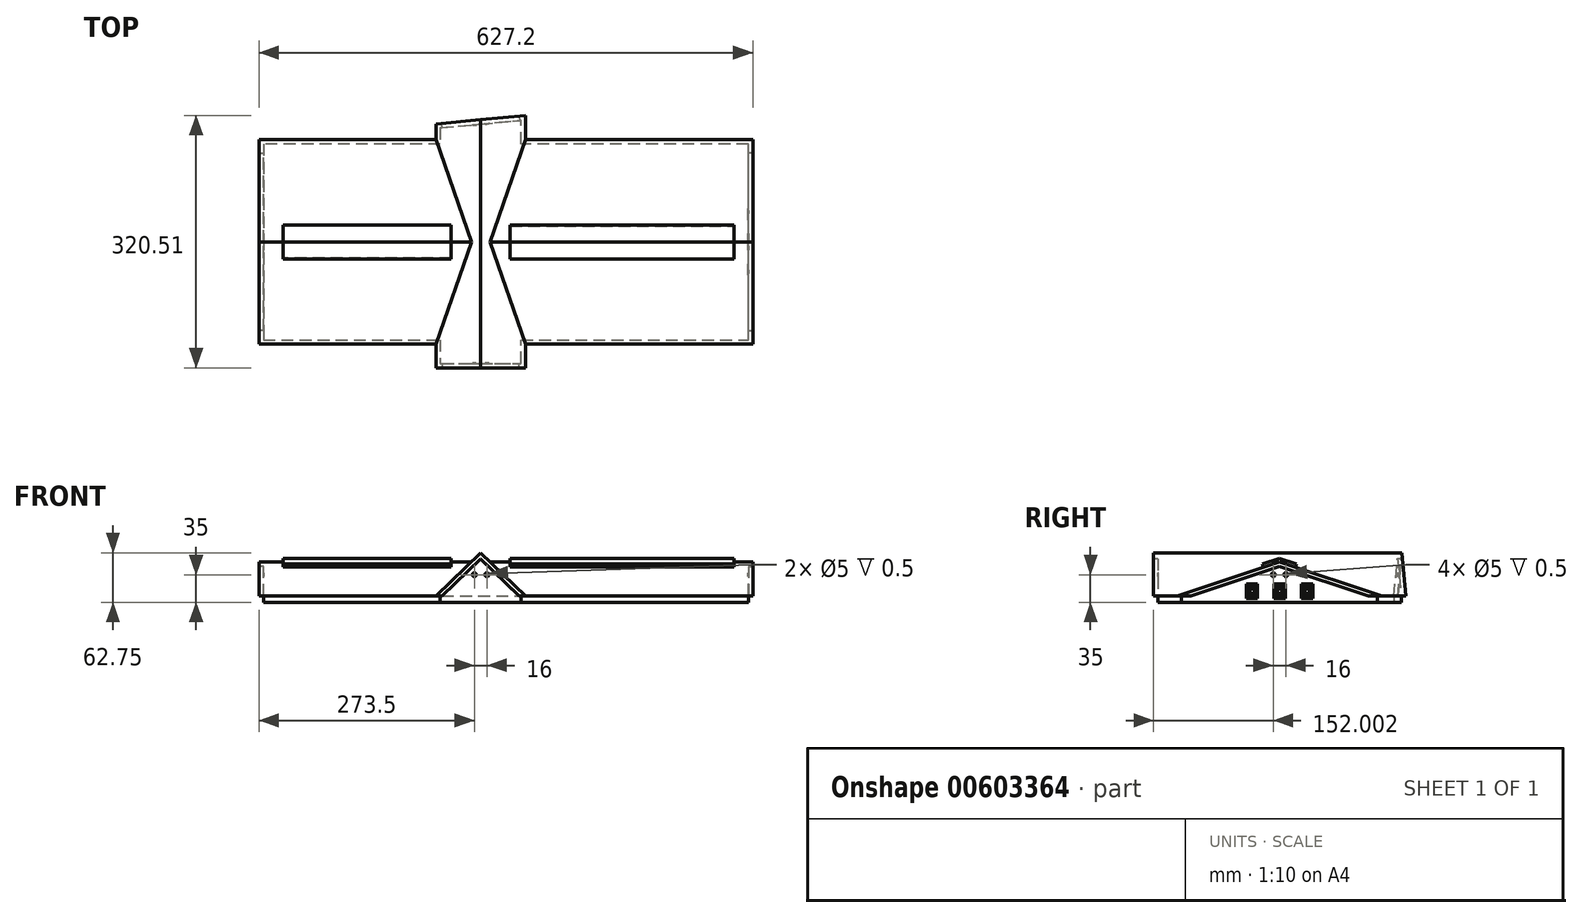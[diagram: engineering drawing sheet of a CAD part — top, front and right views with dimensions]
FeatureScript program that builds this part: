
annotation { "Feature Type Name" : "Feature", "Feature Type Description" : "" }
export const myFeature = defineFeature(function(context is Context, id is Id, definition is map)
    precondition{}
    {
        {
            var Q0;
            Q0=qCreatedBy(makeId("Top.planeOp"),FACE);
            var sketch = newSketch(context, id + "F0", { "sketchPlane" : qUnion([Q0])});
            skLineSegment(sketch, "E0", {"start": v(-327.3, -140.86) * mm, "end": v(-102.6, -140.86) * mm});
            skLineSegment(sketch, "E1", {"start": v(-102.6, -140.86) * mm, "end": v(-102.6, -170.86) * mm});
            skLineSegment(sketch, "E2", {"start": v(-102.6, -170.86) * mm, "end": v(0, -170.86) * mm});
            skLineSegment(sketch, "E3", {"start": v(0, -170.86) * mm, "end": v(0, -140.86) * mm});
            skLineSegment(sketch, "E4", {"start": v(0, -140.86) * mm, "end": v(288.9, -140.86) * mm});
            skLineSegment(sketch, "E5", {"start": v(288.9, -140.86) * mm, "end": v(288.9, 108.14) * mm});
            skLineSegment(sketch, "E6", {"start": v(288.9, 108.14) * mm, "end": v(0, 108.14) * mm});
            skLineSegment(sketch, "E7", {"start": v(0, 108.14) * mm, "end": v(0, 138.14) * mm});
            skLineSegment(sketch, "E8", {"start": v(-102.6, 128.64) * mm, "end": v(-102.6, 108.14) * mm});
            skLineSegment(sketch, "E9", {"start": v(-102.6, 108.14) * mm, "end": v(-327.3, 108.14) * mm});
            skLineSegment(sketch, "E10", {"start": v(-327.3, 108.14) * mm, "end": v(-327.3, -140.86) * mm});
            skLineSegment(sketch, "E11", {"start": v(-102.6, 128.64) * mm, "end": v(0, 138.14) * mm});
            skSolve(sketch);
        }
        {
            var Q0;
            Q0=makeQuery(id+"F0.imprint","IMPRINT",FACE,{"disambiguationData":[TD([[makeQuery(id+"F0.imprint","IMPRINT",EDGE,{"derivedFrom":sQuery(id+"F0.wireOp",EDGE,"E0")}),1.0]])]});
            extrude(context, id + "F1", {"entities" : qUnion([Q0]), "depth" : 8 * mm, "offsetDistance" : 25 * mm});
        }
        {
            var Q0;
            Q0=makeQuery(id+"F1.opExtrude","SWEPT_FACE",FACE,{"disambiguationData":[OSD([sQuery(id+"F0.wireOp",EDGE,"E5")])]});
            var sketch = newSketch(context, id + "F2", { "sketchPlane" : qUnion([Q0])});
            skLineSegment(sketch, "E12", {"start": v(-146.36, 8) * mm, "end": v(113.64, 8) * mm});
            skPoint(sketch, "E13", {"position": v(-140.86, 8) * mm});
            skPoint(sketch, "E14", {"position": v(108.14, 8) * mm});
            skLineSegment(sketch, "E15", {"start": v(-146.36, 8) * mm, "end": v(-16.36, 51.45) * mm});
            skLineSegment(sketch, "E16", {"start": v(-16.36, 51.45) * mm, "end": v(113.64, 8) * mm});
            skPoint(sketch, "E17", {"position": v(-16.36, 8) * mm});
            skSolve(sketch);
        }
        {
            var Q0;
            {var subQ0=sQuery(id+"F2.wireOp",EDGE,"E15");Q0=makeQuery(id+"F2.imprint","IMPRINT",FACE,{"disambiguationData":[TD([[makeQuery(id+"F2.imprint","IMPRINT",EDGE,{"derivedFrom":subQ0}),-1.0]])]});}
            extrude(context, id + "F3", {"entities" : qUnion([Q0]), "operationType" : NewBodyOperationType.ADD, "oppositeDirection" : true, "depth" : (616.2 + 5.5) * mm, "offsetDistance" : 25 * mm});
        }
        {
            var Q0;
            Q0 = qSketchRegion(id + "F2", true);
            extrude(context, id + "F4", {"entities" : qUnion([Q0]), "operationType" : NewBodyOperationType.ADD, "depth" : 5.5 * mm, "offsetDistance" : 25 * mm});
        }
        {
            var Q0;
            Q0=makeQuery(id+"F1.opExtrude","SWEPT_FACE",FACE,{"disambiguationData":[OSD([sQuery(id+"F0.wireOp",EDGE,"E2")])]});
            var sketch = newSketch(context, id + "F5", { "sketchPlane" : qUnion([Q0])});
            skLineSegment(sketch, "E18", {"start": v(-108.1, 8) * mm, "end": v(5.5, 8) * mm});
            skPoint(sketch, "E19", {"position": v(-102.6, 8) * mm});
            skPoint(sketch, "E20", {"position": v(0, 8) * mm});
            skPoint(sketch, "E21", {"position": v(-51.3, 8) * mm});
            skLineSegment(sketch, "E22", {"start": v(-51.3, 8) * mm, "end": v(-51.3, 90.85) * mm, "construction": true});
            skPoint(sketch, "E23", {"position": v(-51.3, 62.75) * mm});
            skLineSegment(sketch, "E24", {"start": v(-108.1, 8) * mm, "end": v(-51.3, 62.75) * mm});
            skLineSegment(sketch, "E25", {"start": v(-51.3, 62.75) * mm, "end": v(5.5, 8) * mm});
            skSolve(sketch);
        }
        {
            var Q0;
            Q0 = qSketchRegion(id + "F5", true);
            var Q1;
            Q1=makeQuery(id+"F1.opExtrude","SWEPT_FACE",FACE,{"disambiguationData":[OSD([sQuery(id+"F0.wireOp",EDGE,"E11")])]});
            extrude(context, id + "F6", {"entities" : qUnion([Q0]), "operationType" : NewBodyOperationType.ADD, "endBound" : BoundingType.UP_TO_SURFACE, "oppositeDirection" : true, "depth" : 25 * mm, "endBoundEntityFace" : qUnion([Q1]), "hasOffset" : true, "offsetDistance" : -5.5 * mm});
        }
        {
            var Q0;
            Q0 = qSketchRegion(id + "F5", true);
            extrude(context, id + "F7", {"entities" : qUnion([Q0]), "operationType" : NewBodyOperationType.ADD, "depth" : 5.5 * mm, "offsetDistance" : 25 * mm});
        }
        {
            var Q0;
            Q0=makeQuery(id+"F6.opExtrude","CAP_FACE",FACE,{"disambiguationData":[OSD([sQuery(id+"F5.wireOp",EDGE,"E18"),sQuery(id+"F5.wireOp",EDGE,"E24"),sQuery(id+"F5.wireOp",EDGE,"E25")])],"isStart":false});
            var sketch = newSketch(context, id + "F8", { "sketchPlane" : qUnion([Q0])});
            skLineSegment(sketch, "E26.0", {"start": v(38.28, 55.82) * mm, "end": v(-15.3, 4.4) * mm});
            skLineSegment(sketch, "E26.1", {"start": v(91.86, 4.4) * mm, "end": v(38.28, 55.82) * mm});
            skLineSegment(sketch, "E27", {"start": v(-15.3, 4.4) * mm, "end": v(91.86, 4.4) * mm});
            skSolve(sketch);
        }
        {
            var Q0;
            {var subQ0=sQuery(id+"F8.wireOp",EDGE,"E26.1");var subQ1=sQuery(id+"F8.wireOp",EDGE,"E26.0");var subQ2=makeQuery(id+"F8.imprint","INTERSECT",VERTEX,{"derivedFrom":[subQ1,subQ0]});Q0=makeQuery(id+"F8.imprint","IMPRINT",FACE,{"disambiguationData":[TD([[makeQuery(id+"F8.imprint","IMPRINT",EDGE,{"disambiguationData":[TD([[subQ2,-1.0]])],"derivedFrom":subQ1}),1.0]])]});}
            extrude(context, id + "F9", {"entities" : qUnion([Q0]), "operationType" : NewBodyOperationType.REMOVE, "oppositeDirection" : true, "depth" : 5.5 * mm, "offsetDistance" : 25 * mm});
        }
        {
            var Q0;
            Q0=makeQuery(id+"F3.opExtrude","CAP_FACE",FACE,{"disambiguationData":[OSD([sQuery(id+"F2.wireOp",EDGE,"E12"),sQuery(id+"F2.wireOp",EDGE,"E15"),sQuery(id+"F2.wireOp",EDGE,"E16")])],"isStart":false});
            var sketch = newSketch(context, id + "F10", { "sketchPlane" : qUnion([Q0])});
            skLineSegment(sketch, "E28.0", {"start": v(16.36, 45.65) * mm, "end": v(-111.9, 2.78) * mm});
            skLineSegment(sketch, "E28.1", {"start": v(144.61, 2.78) * mm, "end": v(16.36, 45.65) * mm});
            skLineSegment(sketch, "E29", {"start": v(-111.9, 2.78) * mm, "end": v(144.61, 2.78) * mm});
            skSolve(sketch);
        }
        {
            var Q0;
            Q0 = qSketchRegion(id + "F10", true);
            extrude(context, id + "F11", {"entities" : qUnion([Q0]), "operationType" : NewBodyOperationType.REMOVE, "oppositeDirection" : true, "depth" : 5.5 * mm, "offsetDistance" : 25 * mm});
        }
        {
            var Q0;
            Q0=makeQuery(id+"F4.opExtrude","CAP_FACE",FACE,{"disambiguationData":[OSD([sQuery(id+"F2.wireOp",EDGE,"E12"),sQuery(id+"F2.wireOp",EDGE,"E15"),sQuery(id+"F2.wireOp",EDGE,"E16")])],"isStart":false});
            var sketch = newSketch(context, id + "F12", { "sketchPlane" : qUnion([Q0])});
            skLineSegment(sketch, "E30.0", {"start": v(-16.36, 45.65) * mm, "end": v(111.9, 2.78) * mm});
            skLineSegment(sketch, "E30.1", {"start": v(-144.61, 2.78) * mm, "end": v(-16.36, 45.65) * mm});
            skLineSegment(sketch, "E31", {"start": v(-144.61, 2.78) * mm, "end": v(111.9, 2.78) * mm});
            skSolve(sketch);
        }
        {
            var Q0;
            Q0 = qSketchRegion(id + "F12", true);
            extrude(context, id + "F13", {"entities" : qUnion([Q0]), "operationType" : NewBodyOperationType.REMOVE, "oppositeDirection" : true, "depth" : 5.5 * mm, "offsetDistance" : 25 * mm});
        }
        {
            var Q0;
            Q0=makeQuery(id+"F7.opExtrude","CAP_FACE",FACE,{"disambiguationData":[OSD([sQuery(id+"F5.wireOp",EDGE,"E18"),sQuery(id+"F5.wireOp",EDGE,"E24"),sQuery(id+"F5.wireOp",EDGE,"E25")])],"isStart":false});
            var sketch = newSketch(context, id + "F14", { "sketchPlane" : qUnion([Q0])});
            skLineSegment(sketch, "E32.0", {"start": v(-51.3, 55.11) * mm, "end": v(1.68, 4.04) * mm});
            skLineSegment(sketch, "E32.1", {"start": v(-104.28, 4.04) * mm, "end": v(-51.3, 55.11) * mm});
            skLineSegment(sketch, "E33", {"start": v(-104.28, 4.04) * mm, "end": v(1.68, 4.04) * mm});
            skSolve(sketch);
        }
        {
            var Q0;
            Q0 = qSketchRegion(id + "F14", true);
            extrude(context, id + "F15", {"entities" : qUnion([Q0]), "operationType" : NewBodyOperationType.REMOVE, "oppositeDirection" : true, "depth" : 5.5 * mm, "offsetDistance" : 25 * mm});
        }
        {
            var Q0;
            Q0=makeQuery(id+"F4.opExtrude","CAP_FACE",FACE,{"disambiguationData":[OSD([sQuery(id+"F2.wireOp",EDGE,"E12"),sQuery(id+"F2.wireOp",EDGE,"E15"),sQuery(id+"F2.wireOp",EDGE,"E16")])],"isStart":false});
            var sketch = newSketch(context, id + "F16", { "sketchPlane" : qUnion([Q0])});
            skLineSegment(sketch, "E34", {"start": v(-36.64, 44.67) * mm, "end": v(-16.36, 51.45) * mm});
            skLineSegment(sketch, "E35", {"start": v(-16.36, 51.45) * mm, "end": v(3.93, 44.67) * mm});
            skLineSegment(sketch, "E36.0", {"start": v(-16.36, 55.67) * mm, "end": v(5.2, 48.47) * mm});
            skLineSegment(sketch, "E36.1", {"start": v(-37.91, 48.47) * mm, "end": v(-16.36, 55.67) * mm});
            skLineSegment(sketch, "E37", {"start": v(-37.91, 48.47) * mm, "end": v(-36.64, 44.67) * mm});
            skLineSegment(sketch, "E38", {"start": v(5.2, 48.47) * mm, "end": v(3.93, 44.67) * mm});
            skSolve(sketch);
        }
        {
            var Q0;
            Q0=makeQuery(id+"F16.imprint","IMPRINT",FACE,{"disambiguationData":[TD([[makeQuery(id+"F16.imprint","IMPRINT",EDGE,{"derivedFrom":sQuery(id+"F16.wireOp",EDGE,"E34")}),1.0]])]});
            extrude(context, id + "F17", {"entities" : qUnion([Q0]), "operationType" : NewBodyOperationType.ADD, "oppositeDirection" : true, "depth" : (30.35 + 277.85) * mm, "offsetDistance" : 25 * mm});
        }
        {
            var Q0;
            Q0 = qSketchRegion(id + "F16", true);
            extrude(context, id + "F18", {"entities" : qUnion([Q0]), "operationType" : NewBodyOperationType.REMOVE, "oppositeDirection" : true, "depth" : 24 * mm, "offsetDistance" : 25 * mm});
        }
        {
            var Q0;
            Q0=makeQuery(id+"F3.opExtrude","CAP_FACE",FACE,{"disambiguationData":[OSD([sQuery(id+"F2.wireOp",EDGE,"E12"),sQuery(id+"F2.wireOp",EDGE,"E15"),sQuery(id+"F2.wireOp",EDGE,"E16")])],"isStart":false});
            var sketch = newSketch(context, id + "F19", { "sketchPlane" : qUnion([Q0])});
            skLineSegment(sketch, "E39", {"start": v(-3.93, 44.67) * mm, "end": v(16.36, 51.45) * mm});
            skLineSegment(sketch, "E40", {"start": v(16.36, 51.45) * mm, "end": v(36.64, 44.67) * mm});
            skLineSegment(sketch, "E41.0", {"start": v(16.36, 55.67) * mm, "end": v(37.91, 48.47) * mm});
            skLineSegment(sketch, "E41.1", {"start": v(-5.2, 48.47) * mm, "end": v(16.36, 55.67) * mm});
            skLineSegment(sketch, "E42", {"start": v(-5.2, 48.47) * mm, "end": v(-3.93, 44.67) * mm});
            skLineSegment(sketch, "E43", {"start": v(37.91, 48.47) * mm, "end": v(36.64, 44.67) * mm});
            skSolve(sketch);
        }
        {
            var Q0;
            Q0 = qSketchRegion(id + "F19", true);
            extrude(context, id + "F20", {"entities" : qUnion([Q0]), "operationType" : NewBodyOperationType.ADD, "oppositeDirection" : true, "depth" : (30.35 + 213.85) * mm, "offsetDistance" : 25 * mm});
        }
        {
            var Q0;
            Q0 = qSketchRegion(id + "F19", true);
            extrude(context, id + "F21", {"entities" : qUnion([Q0]), "operationType" : NewBodyOperationType.REMOVE, "oppositeDirection" : true, "depth" : 30.35 * mm, "offsetDistance" : 25 * mm});
        }
        {
            var Q0;
            Q0=makeQuery(id+"F11.boolean.opBoolean","MERGE",FACE,{"derivedFrom":[makeQuery(id+"F1.opExtrude","SWEPT_FACE",FACE,{"disambiguationData":[OSD([sQuery(id+"F0.wireOp",EDGE,"E10")])]}),makeQuery(id+"F11.opExtrude","CAP_FACE",FACE,{"disambiguationData":[OSD([sQuery(id+"F10.wireOp",EDGE,"E28.0"),sQuery(id+"F10.wireOp",EDGE,"E28.1"),sQuery(id+"F10.wireOp",EDGE,"E29")])],"isStart":false})]});
            var sketch = newSketch(context, id + "F22", { "sketchPlane" : qUnion([Q0])});
            skPoint(sketch, "E44", {"position": v(16.36, 0) * mm});
            skLineSegment(sketch, "E45", {"start": v(16.36, 0) * mm, "end": v(16.36, 35) * mm, "construction": true});
            skLineSegment(sketch, "E46", {"start": v(-4.2, 35) * mm, "end": v(35.76, 35) * mm, "construction": true});
            skPoint(sketch, "E47", {"position": v(8.36, 35) * mm});
            skPoint(sketch, "E48", {"position": v(24.36, 35) * mm});
            skCircle(sketch, "E49", {"center": v(8.36, 35) * mm, "radius": 2.5 * mm});
            skCircle(sketch, "E50", {"center": v(24.36, 35) * mm, "radius": 2.5 * mm});
            skSolve(sketch);
        }
        {
            var Q0;
            Q0 = qSketchRegion(id + "F22", true);
            extrude(context, id + "F23", {"entities" : qUnion([Q0]), "operationType" : NewBodyOperationType.REMOVE, "oppositeDirection" : true, "depth" : .5 * mm, "offsetDistance" : 25 * mm});
        }
        {
            var Q0;
            Q0=makeQuery(id+"F13.boolean.opBoolean","MERGE",FACE,{"derivedFrom":[makeQuery(id+"F3.boolean.opBoolean","MERGE",FACE,{"derivedFrom":[makeQuery(id+"F1.opExtrude","SWEPT_FACE",FACE,{"disambiguationData":[OSD([sQuery(id+"F0.wireOp",EDGE,"E5")])]}),makeQuery(id+"F3.opExtrude","CAP_FACE",FACE,{"disambiguationData":[OSD([sQuery(id+"F2.wireOp",EDGE,"E12"),sQuery(id+"F2.wireOp",EDGE,"E15"),sQuery(id+"F2.wireOp",EDGE,"E16")])],"isStart":true})]}),makeQuery(id+"F13.opExtrude","CAP_FACE",FACE,{"disambiguationData":[OSD([sQuery(id+"F12.wireOp",EDGE,"E30.0"),sQuery(id+"F12.wireOp",EDGE,"E30.1"),sQuery(id+"F12.wireOp",EDGE,"E31")])],"isStart":false})]});
            var sketch = newSketch(context, id + "F24", { "sketchPlane" : qUnion([Q0])});
            skPoint(sketch, "E51", {"position": v(-16.36, 0) * mm});
            skLineSegment(sketch, "E52", {"start": v(-16.36, 0) * mm, "end": v(-16.36, 35) * mm, "construction": true});
            skLineSegment(sketch, "E53", {"start": v(-48.45, 35) * mm, "end": v(-8.49, 35) * mm, "construction": true});
            skPoint(sketch, "E54", {"position": v(-24.36, 35) * mm});
            skPoint(sketch, "E55", {"position": v(-8.36, 35) * mm});
            skCircle(sketch, "E56", {"center": v(-24.36, 35) * mm, "radius": 2.5 * mm});
            skCircle(sketch, "E57", {"center": v(-8.36, 35) * mm, "radius": 2.5 * mm});
            skSolve(sketch);
        }
        {
            var Q0;
            Q0 = qSketchRegion(id + "F24", true);
            extrude(context, id + "F25", {"entities" : qUnion([Q0]), "operationType" : NewBodyOperationType.REMOVE, "oppositeDirection" : true, "depth" : .5 * mm, "offsetDistance" : 25 * mm});
        }
        {
            var Q0;
            Q0=makeQuery(id+"F15.boolean.opBoolean","MERGE",FACE,{"derivedFrom":[makeQuery(id+"F6.boolean.opBoolean","MERGE",FACE,{"derivedFrom":[makeQuery(id+"F1.opExtrude","SWEPT_FACE",FACE,{"disambiguationData":[OSD([sQuery(id+"F0.wireOp",EDGE,"E2")])]}),makeQuery(id+"F6.opExtrude","CAP_FACE",FACE,{"disambiguationData":[OSD([sQuery(id+"F5.wireOp",EDGE,"E18"),sQuery(id+"F5.wireOp",EDGE,"E24"),sQuery(id+"F5.wireOp",EDGE,"E25")])],"isStart":true})]})],"fromTools":[makeQuery(id+"F15.opExtrude","CAP_FACE",FACE,{"disambiguationData":[OSD([sQuery(id+"F14.wireOp",EDGE,"E32.0"),sQuery(id+"F14.wireOp",EDGE,"E32.1"),sQuery(id+"F14.wireOp",EDGE,"E33")])],"isStart":false})]});
            var sketch = newSketch(context, id + "F26", { "sketchPlane" : qUnion([Q0])});
            skPoint(sketch, "E58", {"position": v(-51.3, 0) * mm});
            skLineSegment(sketch, "E59", {"start": v(-51.3, 0) * mm, "end": v(-51.3, 35) * mm, "construction": true});
            skLineSegment(sketch, "E60", {"start": v(-73.66, 35) * mm, "end": v(-33.7, 35) * mm, "construction": true});
            skPoint(sketch, "E61", {"position": v(-59.3, 35) * mm});
            skPoint(sketch, "E62", {"position": v(-43.3, 35) * mm});
            skCircle(sketch, "E63", {"center": v(-59.3, 35) * mm, "radius": 2.5 * mm});
            skCircle(sketch, "E64", {"center": v(-43.3, 35) * mm, "radius": 2.5 * mm});
            skSolve(sketch);
        }
        {
            var Q0;
            Q0 = qSketchRegion(id + "F26", true);
            extrude(context, id + "F27", {"entities" : qUnion([Q0]), "operationType" : NewBodyOperationType.REMOVE, "oppositeDirection" : true, "depth" : .5 * mm, "offsetDistance" : 25 * mm});
        }
        {
            var Q0;
            Q0=makeQuery(id+"F1.opExtrude","SWEPT_FACE",FACE,{"disambiguationData":[OSD([sQuery(id+"F0.wireOp",EDGE,"E11")])]});
            var sketch = newSketch(context, id + "F28", { "sketchPlane" : qUnion([Q0])});
            skPoint(sketch, "E65", {"position": v(38.78, 0) * mm});
            skLineSegment(sketch, "E66", {"start": v(38.78, 0) * mm, "end": v(38.78, 35) * mm, "construction": true});
            skLineSegment(sketch, "E67", {"start": v(13.04, 35) * mm, "end": v(53, 35) * mm, "construction": true});
            skPoint(sketch, "E68", {"position": v(30.78, 35) * mm});
            skPoint(sketch, "E69", {"position": v(46.78, 35) * mm});
            skCircle(sketch, "E70", {"center": v(30.78, 35) * mm, "radius": 2.5 * mm});
            skCircle(sketch, "E71", {"center": v(46.78, 35) * mm, "radius": 2.5 * mm});
            skSolve(sketch);
        }
        {
            var Q0;
            Q0 = qSketchRegion(id + "F28", true);
            extrude(context, id + "F29", {"entities" : qUnion([Q0]), "operationType" : NewBodyOperationType.REMOVE, "oppositeDirection" : true, "depth" : .5 * mm, "offsetDistance" : 25 * mm});
        }
        {
            var Q0;
            Q0=makeQuery(id+"F13.boolean.opBoolean","MERGE",FACE,{"derivedFrom":[makeQuery(id+"F3.boolean.opBoolean","MERGE",FACE,{"derivedFrom":[makeQuery(id+"F1.opExtrude","SWEPT_FACE",FACE,{"disambiguationData":[OSD([sQuery(id+"F0.wireOp",EDGE,"E5")])]}),makeQuery(id+"F3.opExtrude","CAP_FACE",FACE,{"disambiguationData":[OSD([sQuery(id+"F2.wireOp",EDGE,"E12"),sQuery(id+"F2.wireOp",EDGE,"E15"),sQuery(id+"F2.wireOp",EDGE,"E16")])],"isStart":true})]}),makeQuery(id+"F13.opExtrude","CAP_FACE",FACE,{"disambiguationData":[OSD([sQuery(id+"F12.wireOp",EDGE,"E30.0"),sQuery(id+"F12.wireOp",EDGE,"E30.1"),sQuery(id+"F12.wireOp",EDGE,"E31")])],"isStart":false})]});
            var sketch = newSketch(context, id + "F30", { "sketchPlane" : qUnion([Q0])});
            skPoint(sketch, "E72", {"position": v(-16.36, 0) * mm});
            skLineSegment(sketch, "E73", {"start": v(-16.36, 0) * mm, "end": v(-16.36, 40.85) * mm, "construction": true});
            skLineSegment(sketch, "E74.bottom", {"start": v(-23.43, 23) * mm, "end": v(-9.29, 23) * mm});
            skLineSegment(sketch, "E74.top", {"start": v(-23.43, 5) * mm, "end": v(-9.29, 5) * mm});
            skLineSegment(sketch, "E74.left", {"start": v(-23.43, 23) * mm, "end": v(-23.43, 5) * mm});
            skLineSegment(sketch, "E74.right", {"start": v(-9.29, 23) * mm, "end": v(-9.29, 5) * mm});
            skLineSegment(sketch, "E75.0", {"start": v(-21.5, 21.07) * mm, "end": v(-17.32, 21.07) * mm});
            skLineSegment(sketch, "E75.1", {"start": v(-21.5, 21.07) * mm, "end": v(-21.5, 14.96) * mm});
            skLineSegment(sketch, "E75.2", {"start": v(-21.5, 6.93) * mm, "end": v(-17.32, 6.93) * mm});
            skLineSegment(sketch, "E75.3", {"start": v(-11.21, 21.07) * mm, "end": v(-11.21, 14.96) * mm});
            skLineSegment(sketch, "E76.left", {"start": v(-17.32, 21.07) * mm, "end": v(-17.32, 14.96) * mm});
            skLineSegment(sketch, "E76.right", {"start": v(-15.4, 21.07) * mm, "end": v(-15.4, 14.96) * mm});
            skLineSegment(sketch, "E77.bottom", {"start": v(-11.21, 14.96) * mm, "end": v(-15.4, 14.96) * mm});
            skLineSegment(sketch, "E77.top", {"start": v(-11.21, 13.04) * mm, "end": v(-15.4, 13.04) * mm});
            skLineSegment(sketch, "E78.trimOffspring", {"start": v(-17.32, 14.96) * mm, "end": v(-21.5, 14.96) * mm});
            skLineSegment(sketch, "E79.trimOffspring", {"start": v(-17.32, 13.04) * mm, "end": v(-17.32, 6.93) * mm});
            skLineSegment(sketch, "E80.trimOffspring", {"start": v(-17.32, 13.04) * mm, "end": v(-21.5, 13.04) * mm});
            skLineSegment(sketch, "E81.trimOffspring", {"start": v(-15.4, 13.04) * mm, "end": v(-15.4, 6.93) * mm});
            skLineSegment(sketch, "E82.trimOffspring", {"start": v(-11.21, 13.04) * mm, "end": v(-11.21, 6.93) * mm});
            skLineSegment(sketch, "E83.trimOffspring", {"start": v(-21.5, 13.04) * mm, "end": v(-21.5, 6.93) * mm});
            skLineSegment(sketch, "E84.trimOffspring", {"start": v(-15.4, 21.07) * mm, "end": v(-11.21, 21.07) * mm});
            skLineSegment(sketch, "E85.trimOffspring", {"start": v(-15.4, 6.93) * mm, "end": v(-11.21, 6.93) * mm});
            skPoint(sketch, "E86", {"position": v(-16.36, 23) * mm});
            skLineSegment(sketch, "E87.1.0.0", {"start": v(19.6, 13.04) * mm, "end": v(19.6, 6.93) * mm});
            skPoint(sketch, "E87.1.0.1", {"position": v(18.64, 23) * mm});
            skLineSegment(sketch, "E87.1.0.2", {"start": v(19.6, 6.93) * mm, "end": v(23.79, 6.93) * mm});
            skLineSegment(sketch, "E87.1.0.3", {"start": v(13.5, 13.04) * mm, "end": v(13.5, 6.93) * mm});
            skLineSegment(sketch, "E87.1.0.4", {"start": v(17.68, 13.04) * mm, "end": v(17.68, 6.93) * mm});
            skLineSegment(sketch, "E87.1.0.5", {"start": v(11.57, 5) * mm, "end": v(25.71, 5) * mm});
            skLineSegment(sketch, "E87.1.0.6", {"start": v(11.57, 23) * mm, "end": v(25.71, 23) * mm});
            skLineSegment(sketch, "E87.1.0.7", {"start": v(25.71, 23) * mm, "end": v(25.71, 5) * mm});
            skLineSegment(sketch, "E87.1.0.8", {"start": v(11.57, 23) * mm, "end": v(11.57, 5) * mm});
            skLineSegment(sketch, "E87.1.0.9", {"start": v(23.79, 13.04) * mm, "end": v(23.79, 6.93) * mm});
            skLineSegment(sketch, "E87.1.0.10", {"start": v(23.79, 13.04) * mm, "end": v(19.6, 13.04) * mm});
            skLineSegment(sketch, "E87.1.0.11", {"start": v(17.68, 21.07) * mm, "end": v(17.68, 14.96) * mm});
            skLineSegment(sketch, "E87.1.0.12", {"start": v(13.5, 21.07) * mm, "end": v(17.68, 21.07) * mm});
            skLineSegment(sketch, "E87.1.0.13", {"start": v(19.6, 21.07) * mm, "end": v(19.6, 14.96) * mm});
            skLineSegment(sketch, "E87.1.0.14", {"start": v(13.5, 6.93) * mm, "end": v(17.68, 6.93) * mm});
            skLineSegment(sketch, "E87.1.0.15", {"start": v(23.79, 21.07) * mm, "end": v(23.79, 14.96) * mm});
            skLineSegment(sketch, "E87.1.0.16", {"start": v(17.68, 13.04) * mm, "end": v(13.5, 13.04) * mm});
            skLineSegment(sketch, "E87.1.0.17", {"start": v(17.68, 14.96) * mm, "end": v(13.5, 14.96) * mm});
            skLineSegment(sketch, "E87.1.0.18", {"start": v(23.79, 14.96) * mm, "end": v(19.6, 14.96) * mm});
            skLineSegment(sketch, "E87.1.0.19", {"start": v(19.6, 21.07) * mm, "end": v(23.79, 21.07) * mm});
            skLineSegment(sketch, "E87.1.0.20", {"start": v(13.5, 21.07) * mm, "end": v(13.5, 14.96) * mm});
            skLineSegment(sketch, "E87.direction1", {"start": v(-23.43, 5) * mm, "end": v(11.57, 5) * mm, "construction": true});
            skLineSegment(sketch, "E88.1.0.0", {"start": v(-50.4, 6.93) * mm, "end": v(-46.21, 6.93) * mm});
            skPoint(sketch, "E88.1.0.1", {"position": v(-51.36, 0) * mm});
            skLineSegment(sketch, "E88.1.0.2", {"start": v(-58.43, 5) * mm, "end": v(-44.29, 5) * mm});
            skLineSegment(sketch, "E88.1.0.3", {"start": v(-44.29, 23) * mm, "end": v(-44.29, 5) * mm});
            skLineSegment(sketch, "E88.1.0.4", {"start": v(-58.43, 23) * mm, "end": v(-58.43, 5) * mm});
            skLineSegment(sketch, "E88.1.0.5", {"start": v(-46.21, 21.07) * mm, "end": v(-46.21, 14.96) * mm});
            skLineSegment(sketch, "E88.1.0.6", {"start": v(-56.5, 6.93) * mm, "end": v(-52.32, 6.93) * mm});
            skPoint(sketch, "E88.1.0.7", {"position": v(-51.36, 23) * mm});
            skLineSegment(sketch, "E88.1.0.8", {"start": v(-50.4, 13.04) * mm, "end": v(-50.4, 6.93) * mm});
            skLineSegment(sketch, "E88.1.0.9", {"start": v(-52.32, 13.04) * mm, "end": v(-56.5, 13.04) * mm});
            skLineSegment(sketch, "E88.1.0.10", {"start": v(-52.32, 13.04) * mm, "end": v(-52.32, 6.93) * mm});
            skLineSegment(sketch, "E88.1.0.11", {"start": v(-58.43, 23) * mm, "end": v(-44.29, 23) * mm});
            skLineSegment(sketch, "E88.1.0.12", {"start": v(-52.32, 14.96) * mm, "end": v(-56.5, 14.96) * mm});
            skLineSegment(sketch, "E88.1.0.13", {"start": v(-46.21, 13.04) * mm, "end": v(-50.4, 13.04) * mm});
            skLineSegment(sketch, "E88.1.0.14", {"start": v(-46.21, 14.96) * mm, "end": v(-50.4, 14.96) * mm});
            skLineSegment(sketch, "E88.1.0.15", {"start": v(-50.4, 21.07) * mm, "end": v(-46.21, 21.07) * mm});
            skLineSegment(sketch, "E88.1.0.16", {"start": v(-56.5, 21.07) * mm, "end": v(-56.5, 14.96) * mm});
            skLineSegment(sketch, "E88.1.0.17", {"start": v(-56.5, 21.07) * mm, "end": v(-52.32, 21.07) * mm});
            skLineSegment(sketch, "E88.1.0.18", {"start": v(-50.4, 21.07) * mm, "end": v(-50.4, 14.96) * mm});
            skLineSegment(sketch, "E88.1.0.19", {"start": v(-52.32, 21.07) * mm, "end": v(-52.32, 14.96) * mm});
            skLineSegment(sketch, "E88.1.0.20", {"start": v(-56.5, 13.04) * mm, "end": v(-56.5, 6.93) * mm});
            skLineSegment(sketch, "E88.1.0.21", {"start": v(-46.21, 13.04) * mm, "end": v(-46.21, 6.93) * mm});
            skLineSegment(sketch, "E88.direction1", {"start": v(-23.43, 5) * mm, "end": v(-58.43, 5) * mm, "construction": true});
            skSolve(sketch);
        }
        {
            var Q0;
            Q0 = qSketchRegion(id + "F30", true);
            extrude(context, id + "F31", {"entities" : qUnion([Q0]), "operationType" : NewBodyOperationType.REMOVE, "oppositeDirection" : true, "depth" : 0.5 * mm, "offsetDistance" : 25 * mm});
        }
    });
